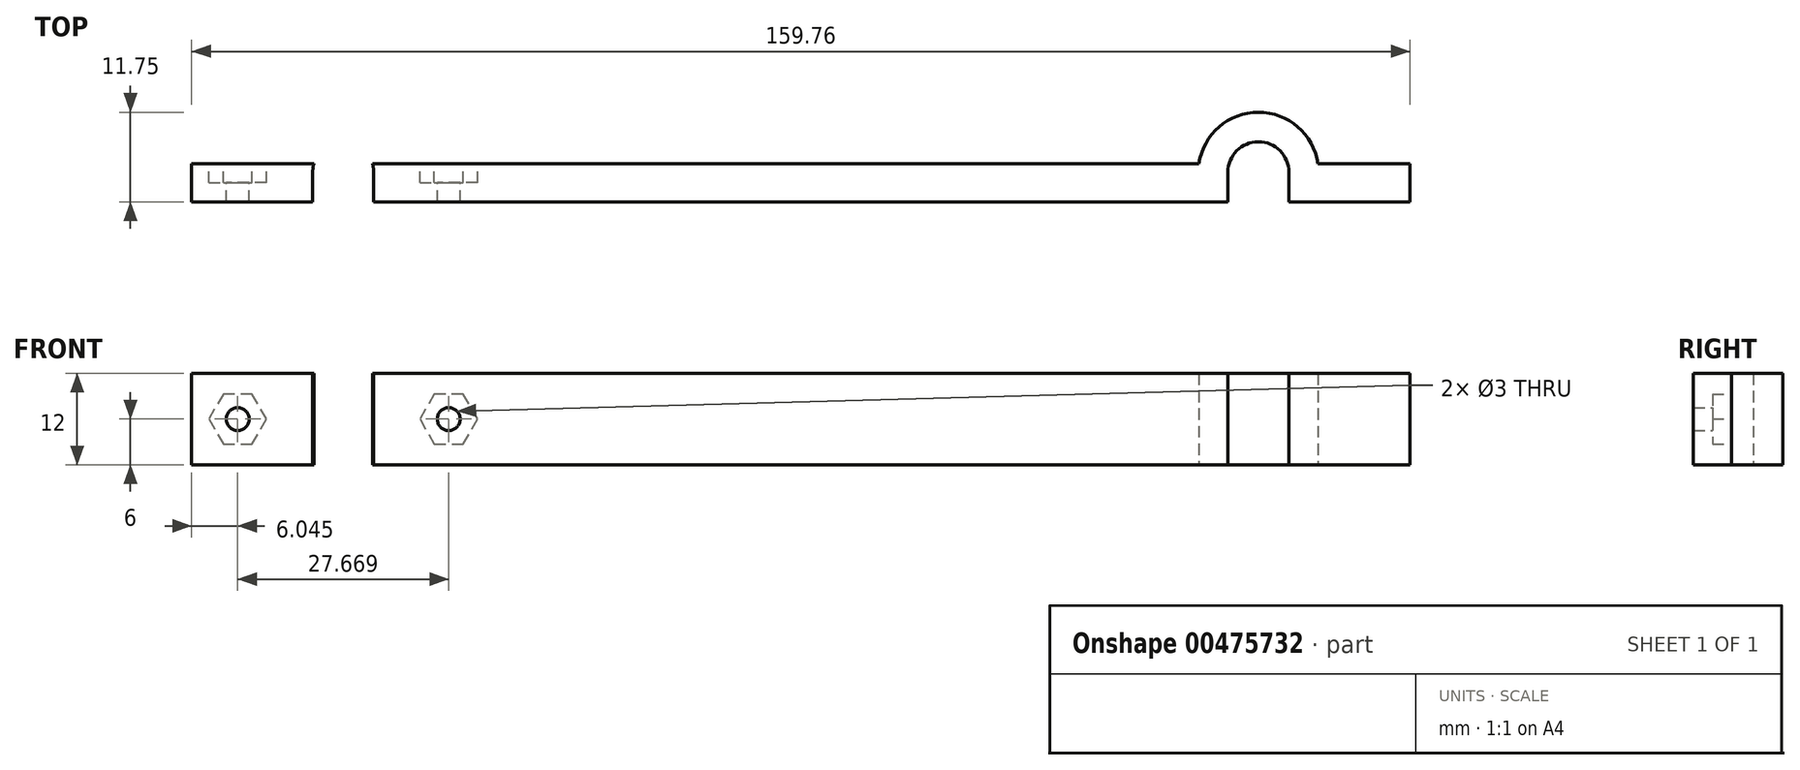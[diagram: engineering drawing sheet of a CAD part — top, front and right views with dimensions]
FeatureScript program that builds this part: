
annotation { "Feature Type Name" : "Feature", "Feature Type Description" : "" }
export const myFeature = defineFeature(function(context is Context, id is Id, definition is map)
    precondition{}
    {
        {
            var Q0;
            Q0=qCreatedBy(makeId("Top.planeOp"),FACE);
            var sketch = newSketch(context, id + "F0", { "sketchPlane" : qUnion([Q0])});
            skLineSegment(sketch, "E0.bottom", {"start": v(-79.88, 5) * mm, "end": v(79.88, 5) * mm});
            skLineSegment(sketch, "E0.top", {"start": v(-79.88, 0) * mm, "end": v(79.88, 0) * mm});
            skLineSegment(sketch, "E0.left", {"start": v(-79.88, 5) * mm, "end": v(-79.88, 0) * mm});
            skLineSegment(sketch, "E0.right", {"start": v(79.88, 5) * mm, "end": v(79.88, 0) * mm});
            skLineSegment(sketch, "E1.bottom", {"start": v(-67.88, 0) * mm, "end": v(-64, 0) * mm});
            skLineSegment(sketch, "E1.top", {"start": v(-67.88, 3.87) * mm, "end": v(-64, 3.87) * mm});
            skLineSegment(sketch, "E1.left", {"start": v(-67.88, 0) * mm, "end": v(-67.88, 3.87) * mm});
            skLineSegment(sketch, "E1.right", {"start": v(-64, 0) * mm, "end": v(-64, 3.88) * mm});
            skLineSegment(sketch, "E2.bottom", {"start": v(-56, 0) * mm, "end": v(-52.12, 0) * mm});
            skLineSegment(sketch, "E2.top", {"start": v(-56, 3.88) * mm, "end": v(-52.12, 3.88) * mm});
            skLineSegment(sketch, "E2.left", {"start": v(-56, 0) * mm, "end": v(-56, 3.88) * mm});
            skLineSegment(sketch, "E2.right", {"start": v(-52.12, 0) * mm, "end": v(-52.12, 3.88) * mm});
            skLineSegment(sketch, "E3.bottom", {"start": v(52.12, 3.88) * mm, "end": v(56, 3.88) * mm});
            skLineSegment(sketch, "E3.top", {"start": v(52.12, 0) * mm, "end": v(56, 0) * mm});
            skLineSegment(sketch, "E3.left", {"start": v(52.12, 3.88) * mm, "end": v(52.12, 0) * mm});
            skLineSegment(sketch, "E3.right", {"start": v(56, 3.87) * mm, "end": v(56, 0) * mm});
            skLineSegment(sketch, "E4.bottom", {"start": v(64, 3.88) * mm, "end": v(67.88, 3.88) * mm});
            skLineSegment(sketch, "E4.top", {"start": v(64, 0) * mm, "end": v(67.88, 0) * mm});
            skLineSegment(sketch, "E4.left", {"start": v(64, 3.88) * mm, "end": v(64, 0) * mm});
            skLineSegment(sketch, "E4.right", {"start": v(67.88, 3.88) * mm, "end": v(67.88, 0) * mm});
            skArc(sketch, "E5", {"start": v(-56, 3.88) * mm, "mid": v(-60, 7.88) * mm, "end": v(-64, 3.88) * mm});
            skArc(sketch, "E6", {"start": v(-52.12, 3.88) * mm, "mid": v(-60, 11.75) * mm, "end": v(-67.88, 3.87) * mm});
            skArc(sketch, "E7", {"start": v(64, 3.88) * mm, "mid": v(60, 7.88) * mm, "end": v(56, 3.87) * mm});
            skArc(sketch, "E8", {"start": v(67.88, 3.88) * mm, "mid": v(60, 11.75) * mm, "end": v(52.13, 3.88) * mm});
            skSolve(sketch);
        }
        {
            var Q0;
            {var subQ0=sQuery(id+"F0.wireOp",EDGE,"E0.left");Q0=makeQuery(id+"F0.imprint","IMPRINT",FACE,{"disambiguationData":[TD([[makeQuery(id+"F0.imprint","IMPRINT",EDGE,{"derivedFrom":subQ0}),1.0]])]});}
            var Q1;
            {var subQ0=sQuery(id+"F0.wireOp",EDGE,"E0.right");Q1=makeQuery(id+"F0.imprint","IMPRINT",FACE,{"disambiguationData":[TD([[makeQuery(id+"F0.imprint","IMPRINT",EDGE,{"derivedFrom":subQ0}),-1.0]])]});}
            var Q2;
            {var subQ0=sQuery(id+"F0.wireOp",EDGE,"E2.right");var subQ1=sQuery(id+"F0.wireOp",EDGE,"E0.bottom");var subQ2=makeQuery(id+"F0.imprint","INTERSECT",VERTEX,{"derivedFrom":[subQ1,subQ0]});Q2=makeQuery(id+"F0.imprint","IMPRINT",FACE,{"disambiguationData":[TD([[makeQuery(id+"F0.imprint","IMPRINT",EDGE,{"disambiguationData":[TD([[subQ2,-1.0]])],"derivedFrom":subQ1}),-1.0]])]});}
            var Q3;
            {var subQ5=sQuery(id+"F0.wireOp",EDGE,"E1.bottom");Q3=makeQuery(id+"F0.imprint","IMPRINT",FACE,{"disambiguationData":[TD([[makeQuery(id+"F0.imprint","IMPRINT",EDGE,{"derivedFrom":subQ5}),1.0]])]});}
            var Q4;
            {var subQ5=sQuery(id+"F0.wireOp",EDGE,"E1.top");Q4=makeQuery(id+"F0.imprint","IMPRINT",FACE,{"disambiguationData":[TD([[makeQuery(id+"F0.imprint","IMPRINT",EDGE,{"derivedFrom":subQ5}),-1.0]])]});}
            var Q5;
            {var subQ5=sQuery(id+"F0.wireOp",EDGE,"E2.bottom");Q5=makeQuery(id+"F0.imprint","IMPRINT",FACE,{"disambiguationData":[TD([[makeQuery(id+"F0.imprint","IMPRINT",EDGE,{"derivedFrom":subQ5}),1.0]])]});}
            var Q6;
            {var subQ5=sQuery(id+"F0.wireOp",EDGE,"E2.top");Q6=makeQuery(id+"F0.imprint","IMPRINT",FACE,{"disambiguationData":[TD([[makeQuery(id+"F0.imprint","IMPRINT",EDGE,{"derivedFrom":subQ5}),-1.0]])]});}
            var Q7;
            {var subQ5=sQuery(id+"F0.wireOp",EDGE,"E3.bottom");Q7=makeQuery(id+"F0.imprint","IMPRINT",FACE,{"disambiguationData":[TD([[makeQuery(id+"F0.imprint","IMPRINT",EDGE,{"derivedFrom":subQ5}),-1.0]])]});}
            var Q8;
            {var subQ5=sQuery(id+"F0.wireOp",EDGE,"E3.top");Q8=makeQuery(id+"F0.imprint","IMPRINT",FACE,{"disambiguationData":[TD([[makeQuery(id+"F0.imprint","IMPRINT",EDGE,{"derivedFrom":subQ5}),1.0]])]});}
            var Q9;
            {var subQ5=sQuery(id+"F0.wireOp",EDGE,"E4.bottom");Q9=makeQuery(id+"F0.imprint","IMPRINT",FACE,{"disambiguationData":[TD([[makeQuery(id+"F0.imprint","IMPRINT",EDGE,{"derivedFrom":subQ5}),-1.0]])]});}
            var Q10;
            {var subQ5=sQuery(id+"F0.wireOp",EDGE,"E4.top");Q10=makeQuery(id+"F0.imprint","IMPRINT",FACE,{"disambiguationData":[TD([[makeQuery(id+"F0.imprint","IMPRINT",EDGE,{"derivedFrom":subQ5}),1.0]])]});}
            var Q11;
            Q11=makeQuery(id+"F0.imprint","IMPRINT",FACE,{"disambiguationData":[TD([[makeQuery(id+"F0.imprint","IMPRINT",EDGE,{"derivedFrom":sQuery(id+"F0.wireOp",EDGE,"E1.top")}),1.0]])]});
            var Q12;
            Q12=makeQuery(id+"F0.imprint","IMPRINT",FACE,{"disambiguationData":[TD([[makeQuery(id+"F0.imprint","IMPRINT",EDGE,{"derivedFrom":sQuery(id+"F0.wireOp",EDGE,"E3.bottom")}),1.0]])]});
            var Q13;
            {var subQ0=sQuery(id+"F0.wireOp",EDGE,"E8");var subQ1=sQuery(id+"F0.wireOp",EDGE,"E0.bottom");var subQ2=makeQuery(id+"F0.imprint","INTERSECT",VERTEX,{"disambiguationData":[OD(0.0)],"derivedFrom":[subQ1,subQ0]});Q13=makeQuery(id+"F0.imprint","IMPRINT",FACE,{"disambiguationData":[TD([[makeQuery(id+"F0.imprint","IMPRINT",EDGE,{"disambiguationData":[TD([[subQ2,-1.0]])],"derivedFrom":subQ1}),1.0]])]});}
            var Q14;
            {var subQ0=sQuery(id+"F0.wireOp",EDGE,"E2.right");Q14=makeQuery(id+"F0.imprint","IMPRINT",FACE,{"disambiguationData":[TD([[makeQuery(id+"F0.imprint","IMPRINT",EDGE,{"derivedFrom":subQ0}),-1.0]])]});}
            var Q15;
            {var subQ0=sQuery(id+"F0.wireOp",EDGE,"E6");var subQ1=sQuery(id+"F0.wireOp",EDGE,"E0.bottom");var subQ2=makeQuery(id+"F0.imprint","INTERSECT",VERTEX,{"disambiguationData":[OD(0.0)],"derivedFrom":[subQ1,subQ0]});Q15=makeQuery(id+"F0.imprint","IMPRINT",FACE,{"disambiguationData":[TD([[makeQuery(id+"F0.imprint","IMPRINT",EDGE,{"disambiguationData":[TD([[subQ2,-1.0]])],"derivedFrom":subQ1}),1.0]])]});}
            extrude(context, id + "F1", {"entities" : qUnion([Q0, Q1, Q2, Q3, Q4, Q5, Q6, Q7, Q8, Q9, Q10, Q11, Q12, Q13, Q14, Q15]), "depth" : 12 * mm});
        }
        {
            var Q0;
            {var subQ0=sQuery(id+"F0.wireOp",EDGE,"E0.bottom");Q0=makeQuery(id+"F1.opExtrude","SWEPT_FACE",FACE,{"disambiguationData":[OSD([subQ0]),TDD([makeQuery(id+"F0.imprint","IMPRINT",EDGE,{"disambiguationData":[TD([[makeQuery(id+"F0.imprint","INTERSECT",VERTEX,{"derivedFrom":[subQ0,sQuery(id+"F0.wireOp",EDGE,"E2.right")]}),-1.0]])],"derivedFrom":subQ0})])]});}
            var sketch = newSketch(context, id + "F2", { "sketchPlane" : qUnion([Q0])});
            skCircle(sketch, "E9.cCircle", {"center": v(46.17, 6) * mm, "radius": 3.28 * mm, "construction": true});
            skPoint(sketch, "E9.cCircle.centerSnap0", {"position": v(79.88, 6) * mm});
            skLineSegment(sketch, "E9.0", {"start": v(48.06, 2.73) * mm, "end": v(44.27, 2.73) * mm});
            skLineSegment(sketch, "E9.1", {"start": v(44.27, 2.72) * mm, "end": v(42.38, 6) * mm});
            skLineSegment(sketch, "E9.2", {"start": v(42.38, 6) * mm, "end": v(44.27, 9.28) * mm});
            skLineSegment(sketch, "E9.3", {"start": v(44.27, 9.28) * mm, "end": v(48.06, 9.28) * mm});
            skLineSegment(sketch, "E9.4", {"start": v(48.06, 9.28) * mm, "end": v(49.95, 6) * mm});
            skLineSegment(sketch, "E9.5", {"start": v(49.95, 6) * mm, "end": v(48.06, 2.72) * mm});
            skPoint(sketch, "E9.0.midPoint", {"position": v(46.17, 2.73) * mm});
            skCircle(sketch, "E10.cCircle", {"center": v(73.83, 6) * mm, "radius": 3.28 * mm, "construction": true});
            skLineSegment(sketch, "E10.0", {"start": v(75.73, 2.73) * mm, "end": v(71.94, 2.73) * mm});
            skLineSegment(sketch, "E10.1", {"start": v(71.94, 2.73) * mm, "end": v(70.05, 6) * mm});
            skLineSegment(sketch, "E10.2", {"start": v(70.05, 6) * mm, "end": v(71.94, 9.27) * mm});
            skLineSegment(sketch, "E10.3", {"start": v(71.94, 9.27) * mm, "end": v(75.73, 9.27) * mm});
            skLineSegment(sketch, "E10.4", {"start": v(75.73, 9.27) * mm, "end": v(77.62, 6) * mm});
            skLineSegment(sketch, "E10.5", {"start": v(77.62, 6) * mm, "end": v(75.73, 2.73) * mm});
            skPoint(sketch, "E10.0.midPoint", {"position": v(73.83, 2.73) * mm});
            skLineSegment(sketch, "E11", {"start": v(46.17, 6) * mm, "end": v(0, 6) * mm, "construction": true});
            skLineSegment(sketch, "E12", {"start": v(46.17, 6) * mm, "end": v(73.83, 6) * mm, "construction": true});
            skLineSegment(sketch, "E13", {"start": v(60, 6) * mm, "end": v(60, 0) * mm, "construction": true});
            skSolve(sketch);
        }
        {
            var Q0;
            Q0=qSketchRegion(id+"F2",true);
            extrude(context, id + "F3", {"entities" : qUnion([Q0]), "operationType" : NewBodyOperationType.REMOVE, "oppositeDirection" : true, "depth" : 2.5 * mm});
        }
        {
            var Q0;
            {var subQ0=sQuery(id+"F0.wireOp",EDGE,"E0.bottom");Q0=makeQuery(id+"F1.opExtrude","SWEPT_FACE",FACE,{"disambiguationData":[OSD([subQ0]),TDD([makeQuery(id+"F0.imprint","IMPRINT",EDGE,{"disambiguationData":[TD([[makeQuery(id+"F0.imprint","INTERSECT",VERTEX,{"derivedFrom":[subQ0,sQuery(id+"F0.wireOp",EDGE,"E2.right")]}),-1.0]])],"derivedFrom":subQ0})])]});}
            var sketch = newSketch(context, id + "F4", { "sketchPlane" : qUnion([Q0])});
            skCircle(sketch, "E14", {"center": v(46.17, 6) * mm, "radius": 1.5 * mm});
            skPoint(sketch, "E14.centerSnap0", {"position": v(46.17, 2.73) * mm});
            skCircle(sketch, "E15", {"center": v(73.83, 6) * mm, "radius": 1.5 * mm});
            skSolve(sketch);
        }
        {
            var Q0;
            Q0=qSketchRegion(id+"F4",true);
            extrude(context, id + "F5", {"entities" : qUnion([Q0]), "operationType" : NewBodyOperationType.REMOVE, "endBound" : BoundingType.THROUGH_ALL, "oppositeDirection" : true, "depth" : 25 * mm});
        }
    });
